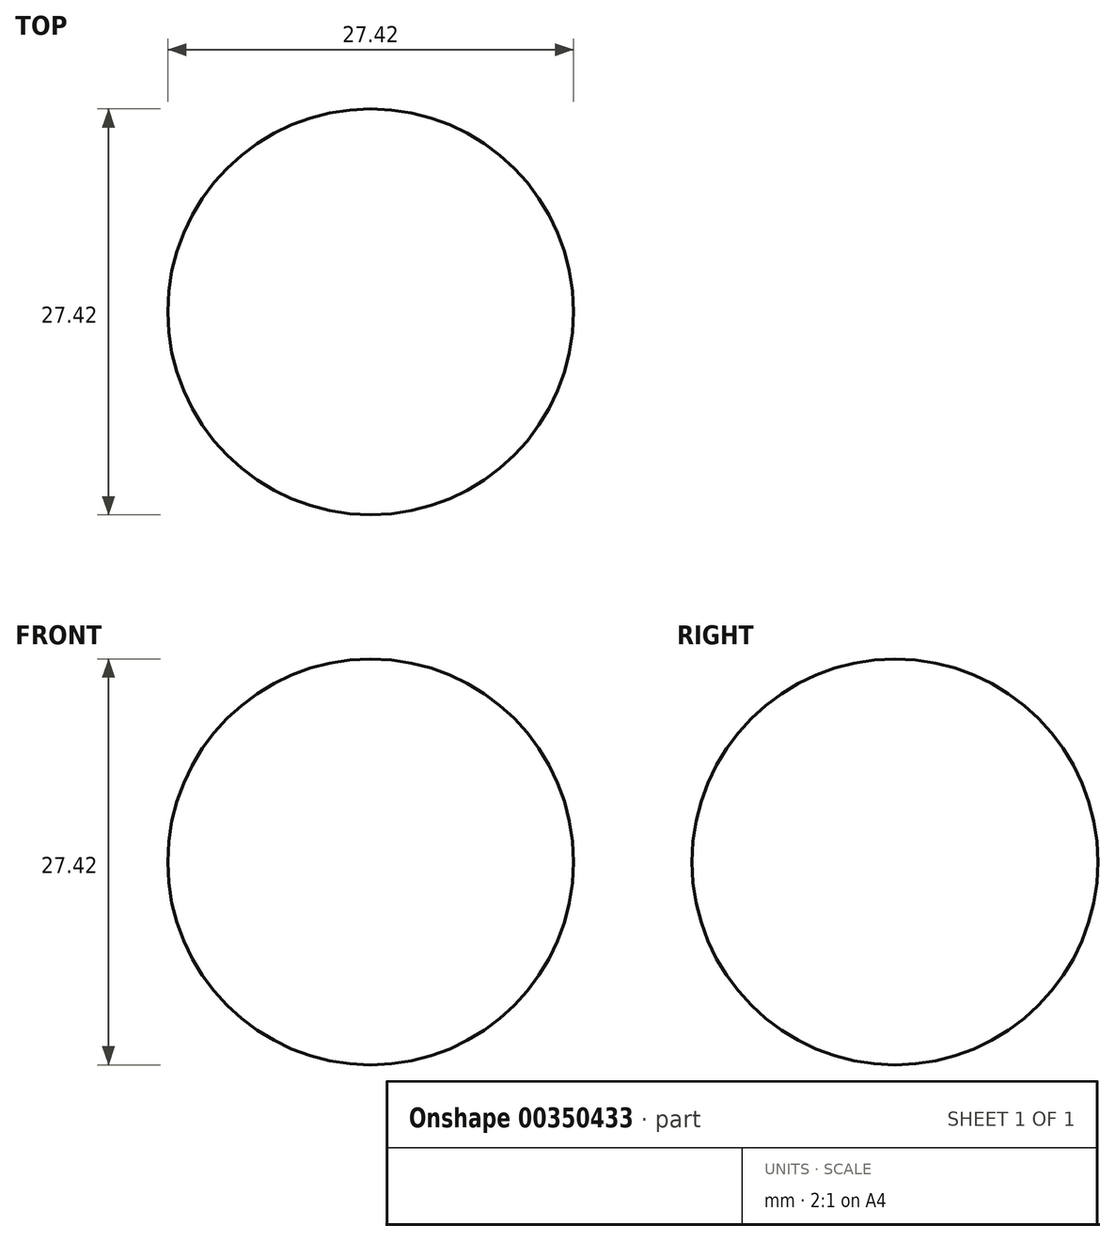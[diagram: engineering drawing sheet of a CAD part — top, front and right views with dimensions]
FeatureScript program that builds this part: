
annotation { "Feature Type Name" : "Feature", "Feature Type Description" : "" }
export const myFeature = defineFeature(function(context is Context, id is Id, definition is map)
    precondition{}
    {
        {
            var Q0;
            Q0=qCreatedBy(makeId("Front.planeOp"),FACE);
            var sketch = newSketch(context, id + "F0", { "sketchPlane" : qUnion([Q0])});
            skArc(sketch, "E0", {"start": v(0, 27.42) * mm, "mid": v(-13.7, 13.7) * mm, "end": v(0, 0) * mm});
            skLineSegment(sketch, "E1", {"start": v(0, 0) * mm, "end": v(0, 27.42) * mm});
            skSolve(sketch);
        }
        {
            var Q0;
            Q0 = qSketchRegion(id + "F0", true);
            var Q1;
            Q1=sQuery(id+"F0.wireOp",EDGE,"E1");
            revolve(context, id + "F1", {"entities" : qUnion([Q0]), "axis" : qUnion([Q1]), "revolveType" : RevolveType.FULL});
        }
    });
